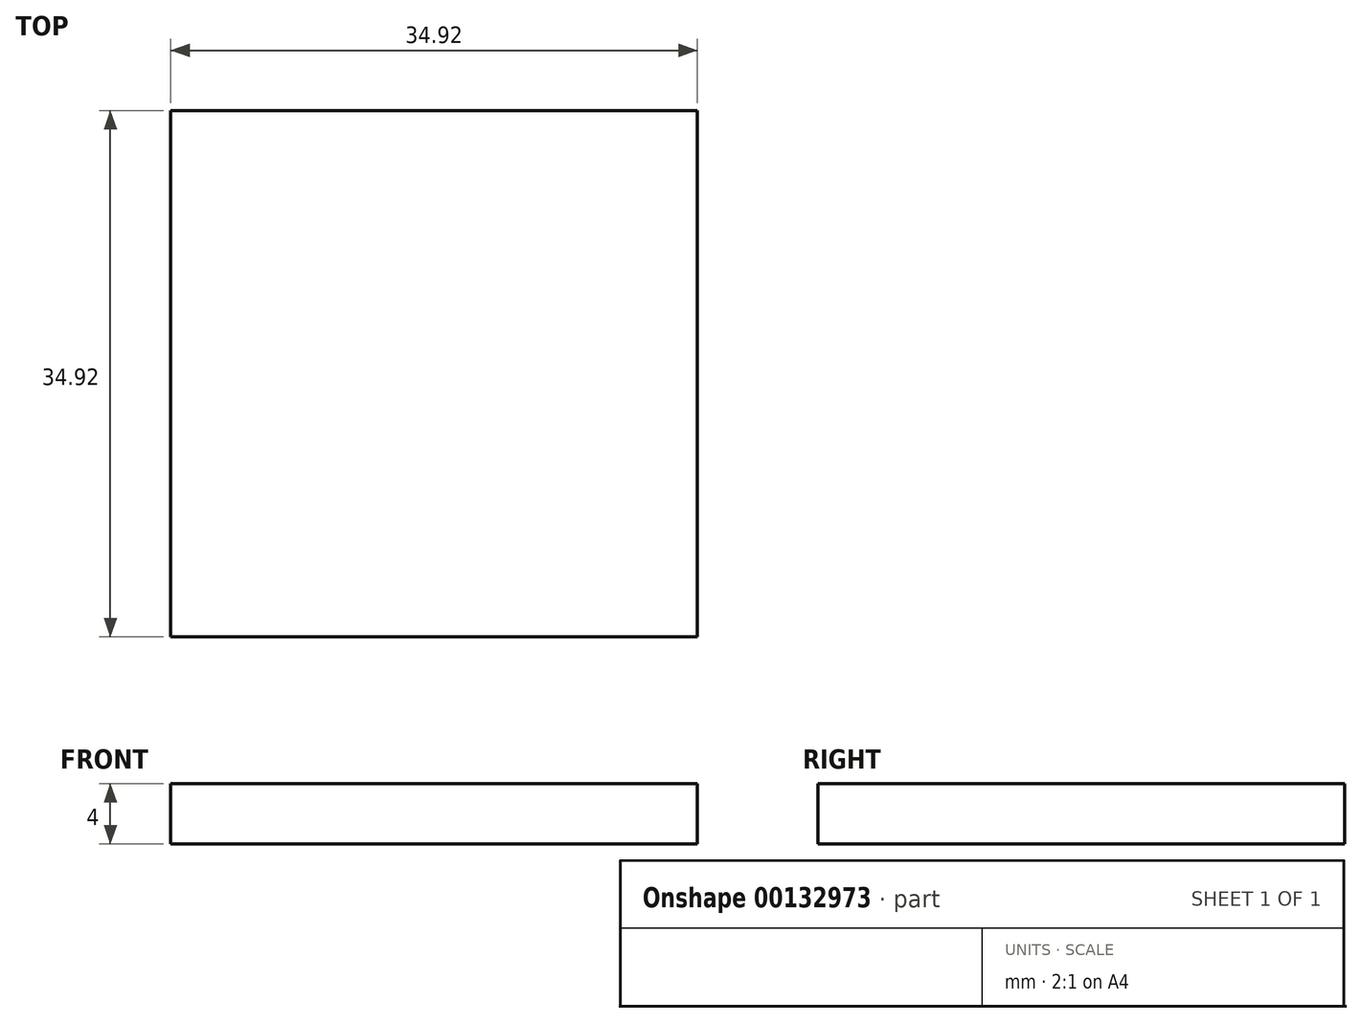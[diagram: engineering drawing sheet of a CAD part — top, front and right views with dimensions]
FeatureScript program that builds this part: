
annotation { "Feature Type Name" : "Feature", "Feature Type Description" : "" }
export const myFeature = defineFeature(function(context is Context, id is Id, definition is map)
    precondition{}
    {
        {
            var Q0;
            Q0=qCreatedBy(makeId("Top.planeOp"),FACE);
            var sketch = newSketch(context, id + "F0", { "sketchPlane" : qUnion([Q0])});
            skLineSegment(sketch, "E0.bottom", {"start": v(-17.46, 17.46) * mm, "end": v(17.46, 17.46) * mm});
            skLineSegment(sketch, "E0.top", {"start": v(-17.46, -17.46) * mm, "end": v(17.46, -17.46) * mm});
            skLineSegment(sketch, "E0.left", {"start": v(-17.46, 17.46) * mm, "end": v(-17.46, -17.46) * mm});
            skLineSegment(sketch, "E0.right", {"start": v(17.46, 17.46) * mm, "end": v(17.46, -17.46) * mm});
            skPoint(sketch, "E1", {"position": v(0, 17.46) * mm});
            skPoint(sketch, "E2", {"position": v(-17.46, 0) * mm});
            skSolve(sketch);
        }
        {
            var Q0;
            Q0=makeQuery(id+"F0.imprint","IMPRINT",FACE,{"disambiguationData":[TD([[makeQuery(id+"F0.imprint","IMPRINT",EDGE,{"derivedFrom":sQuery(id+"F0.wireOp",EDGE,"E0.bottom")}),-1.0]])]});
            extrude(context, id + "F1", {"entities" : qUnion([Q0]), "oppositeDirection" : true, "depth" : 4 * mm});
        }
    });
